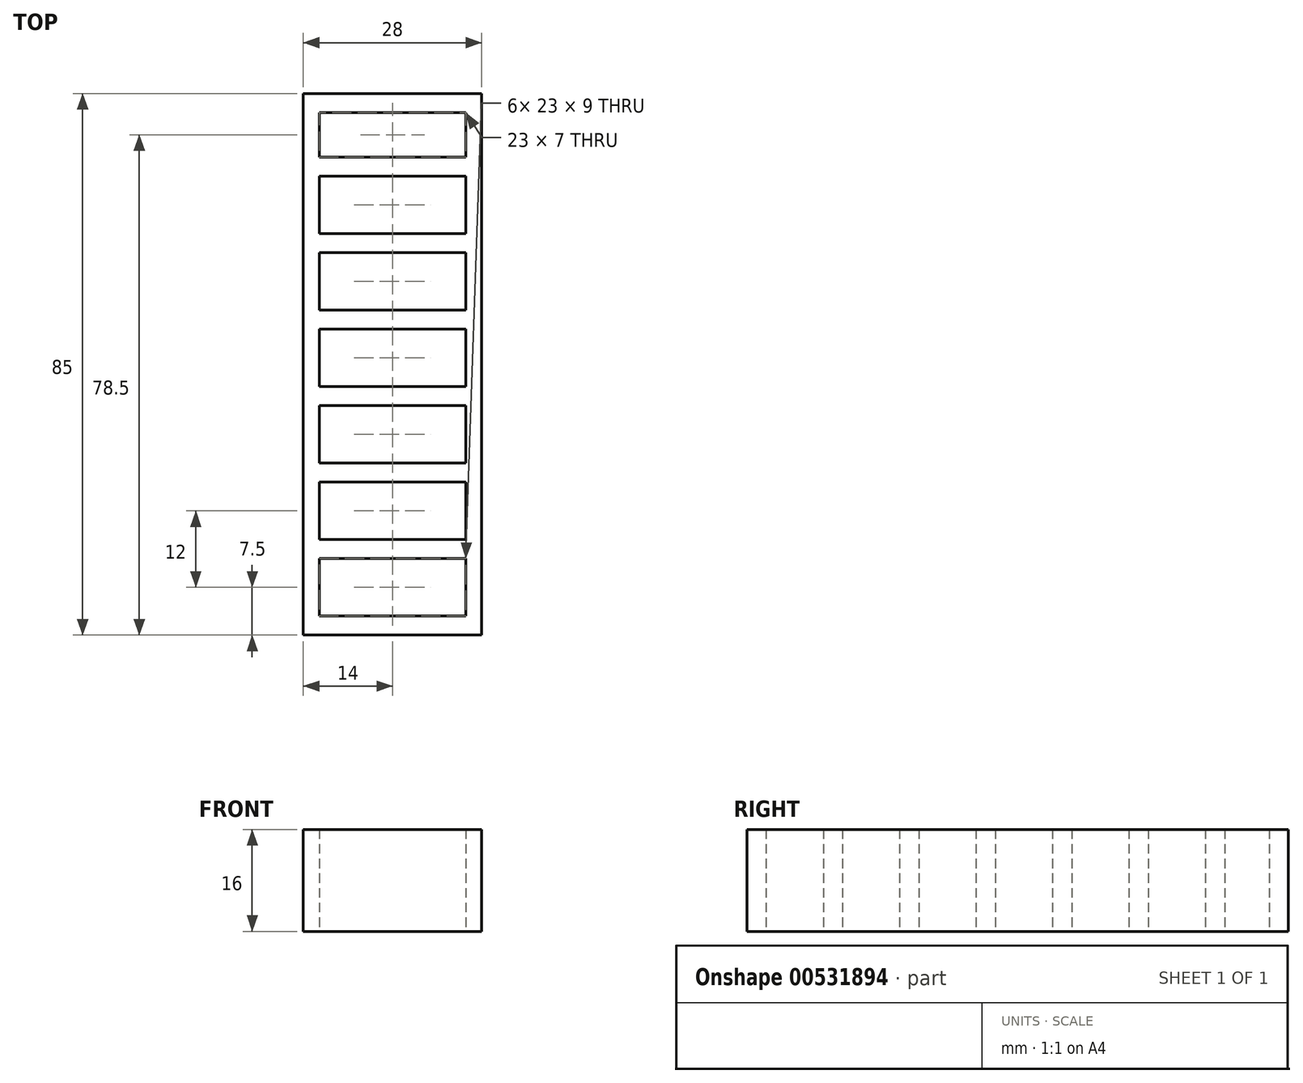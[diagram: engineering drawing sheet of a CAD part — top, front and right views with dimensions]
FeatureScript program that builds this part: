
annotation { "Feature Type Name" : "Feature", "Feature Type Description" : "" }
export const myFeature = defineFeature(function(context is Context, id is Id, definition is map)
    precondition{}
    {
        {
            var Q0;
            Q0=qCreatedBy(makeId("Front.planeOp"),FACE);
            var sketch = newSketch(context, id + "F0", { "sketchPlane" : qUnion([Q0])});
            skLineSegment(sketch, "E0.bottom", {"start": v(14, 8) * mm, "end": v(-14, 8) * mm});
            skLineSegment(sketch, "E0.top", {"start": v(14, -8) * mm, "end": v(-14, -8) * mm});
            skLineSegment(sketch, "E0.left", {"start": v(14, 8) * mm, "end": v(14, -8) * mm});
            skLineSegment(sketch, "E0.right", {"start": v(-14, 8) * mm, "end": v(-14, -8) * mm});
            skPoint(sketch, "E0.middle", {"position": v(0, 0) * mm});
            skSolve(sketch);
        }
        {
            var Q0;
            Q0 = qSketchRegion(id + "F0", true);
            extrude(context, id + "F1", {"entities" : qUnion([Q0]), "depth" : 85 * mm, "offsetDistance" : 25 * mm});
        }
        {
            var Q0;
            Q0=makeQuery(id+"F1.opExtrude","SWEPT_FACE",FACE,{"disambiguationData":[OSD([sQuery(id+"F0.wireOp",EDGE,"E0.top")])]});
            var sketch = newSketch(context, id + "F2", { "sketchPlane" : qUnion([Q0])});
            skLineSegment(sketch, "E1.bottom", {"start": v(11.5, 82) * mm, "end": v(-11.5, 82) * mm});
            skLineSegment(sketch, "E1.top", {"start": v(11.5, 73) * mm, "end": v(-11.5, 73) * mm});
            skLineSegment(sketch, "E1.left", {"start": v(11.5, 82) * mm, "end": v(11.5, 73) * mm});
            skLineSegment(sketch, "E1.right", {"start": v(-11.5, 82) * mm, "end": v(-11.5, 73) * mm});
            skPoint(sketch, "E1.middle", {"position": v(0, 77.5) * mm});
            skLineSegment(sketch, "E2.bottom", {"start": v(11.5, 70) * mm, "end": v(-11.5, 70) * mm});
            skLineSegment(sketch, "E2.top", {"start": v(11.5, 61) * mm, "end": v(-11.5, 61) * mm});
            skLineSegment(sketch, "E2.left", {"start": v(11.5, 70) * mm, "end": v(11.5, 61) * mm});
            skLineSegment(sketch, "E2.right", {"start": v(-11.5, 70) * mm, "end": v(-11.5, 61) * mm});
            skPoint(sketch, "E2.middle", {"position": v(0, 65.5) * mm});
            skLineSegment(sketch, "E3.bottom", {"start": v(11.5, 58) * mm, "end": v(-11.5, 58) * mm});
            skLineSegment(sketch, "E3.top", {"start": v(11.5, 49) * mm, "end": v(-11.5, 49) * mm});
            skLineSegment(sketch, "E3.left", {"start": v(11.5, 58) * mm, "end": v(11.5, 49) * mm});
            skLineSegment(sketch, "E3.right", {"start": v(-11.5, 58) * mm, "end": v(-11.5, 49) * mm});
            skPoint(sketch, "E3.middle", {"position": v(0, 53.5) * mm});
            skLineSegment(sketch, "E4.bottom", {"start": v(11.5, 46) * mm, "end": v(-11.5, 46) * mm});
            skLineSegment(sketch, "E4.top", {"start": v(11.5, 37) * mm, "end": v(-11.5, 37) * mm});
            skLineSegment(sketch, "E4.left", {"start": v(11.5, 46) * mm, "end": v(11.5, 37) * mm});
            skLineSegment(sketch, "E4.right", {"start": v(-11.5, 46) * mm, "end": v(-11.5, 37) * mm});
            skPoint(sketch, "E4.middle", {"position": v(0, 41.5) * mm});
            skLineSegment(sketch, "E5.bottom", {"start": v(11.5, 34) * mm, "end": v(-11.5, 34) * mm});
            skLineSegment(sketch, "E5.top", {"start": v(11.5, 25) * mm, "end": v(-11.5, 25) * mm});
            skLineSegment(sketch, "E5.left", {"start": v(11.5, 34) * mm, "end": v(11.5, 25) * mm});
            skLineSegment(sketch, "E5.right", {"start": v(-11.5, 34) * mm, "end": v(-11.5, 25) * mm});
            skPoint(sketch, "E5.middle", {"position": v(0, 29.5) * mm});
            skLineSegment(sketch, "E6.bottom", {"start": v(11.5, 22) * mm, "end": v(-11.5, 22) * mm});
            skLineSegment(sketch, "E6.top", {"start": v(11.5, 13) * mm, "end": v(-11.5, 13) * mm});
            skLineSegment(sketch, "E6.left", {"start": v(11.5, 22) * mm, "end": v(11.5, 13) * mm});
            skLineSegment(sketch, "E6.right", {"start": v(-11.5, 22) * mm, "end": v(-11.5, 13) * mm});
            skPoint(sketch, "E6.middle", {"position": v(0, 17.5) * mm});
            skLineSegment(sketch, "E7.bottom", {"start": v(11.5, 10) * mm, "end": v(-11.5, 10) * mm});
            skLineSegment(sketch, "E7.top", {"start": v(11.5, 3) * mm, "end": v(-11.5, 3) * mm});
            skLineSegment(sketch, "E7.left", {"start": v(11.5, 10) * mm, "end": v(11.5, 3) * mm});
            skLineSegment(sketch, "E7.right", {"start": v(-11.5, 10) * mm, "end": v(-11.5, 3) * mm});
            skPoint(sketch, "E7.middle", {"position": v(0, 6.5) * mm});
            skPoint(sketch, "E7.middle.positionSnap0", {"position": v(0, 25) * mm});
            skPoint(sketch, "E7.centerSnap0", {"position": v(0, 25) * mm});
            skSolve(sketch);
        }
        {
            var Q0;
            Q0 = qSketchRegion(id + "F2", true);
            extrude(context, id + "F3", {"entities" : qUnion([Q0]), "operationType" : NewBodyOperationType.REMOVE, "oppositeDirection" : true, "depth" : 25 * mm, "offsetDistance" : 25 * mm});
        }
    });
